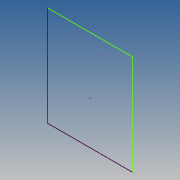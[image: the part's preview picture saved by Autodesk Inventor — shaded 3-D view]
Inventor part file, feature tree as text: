
AUTODESK INVENTOR PART (.ipt)
format: ipt  version: 2019 (Build 230136000, 136)  size: 86,016 bytes
history: native  units: mm
features: reference x6, other x4, extrude x2, sketch x2
ambient origin geometry x8: Origin, YZ Plane, XZ Plane, XY Plane, X Axis, Y Axis, Z Axis, Center Point
bodies: Solid1 (feature_tree)
feature tree (14):
  extrude  "Extrusion1"  Depth=10.0mm
  extrude  "Extrusion2"  [1 undecoded]
  sketch  "Sketch1"  dims[d0=8.0mm d1=0.0mm d2=10.0mm]
  reference  "Reference1"
  reference  "Reference2"
  reference  "Reference3"
  reference  "Reference4"
  reference  "Reference5"
  reference  "Reference6"
  sketch  "Sketch2"  dims[d3=38.0mm d4=0.0mm]
  other  "Assembly1"
  other  "ZFM2020-Stage:2"
  other  "ZFM2020-Stage:3"
  other  "ZFM2020-Stage:1"
note: 1 required parameter value undecoded (feature->parameter linkage not recoverable at this tier; creation-order binding heuristic only, values carry confidence <= 0.55)
